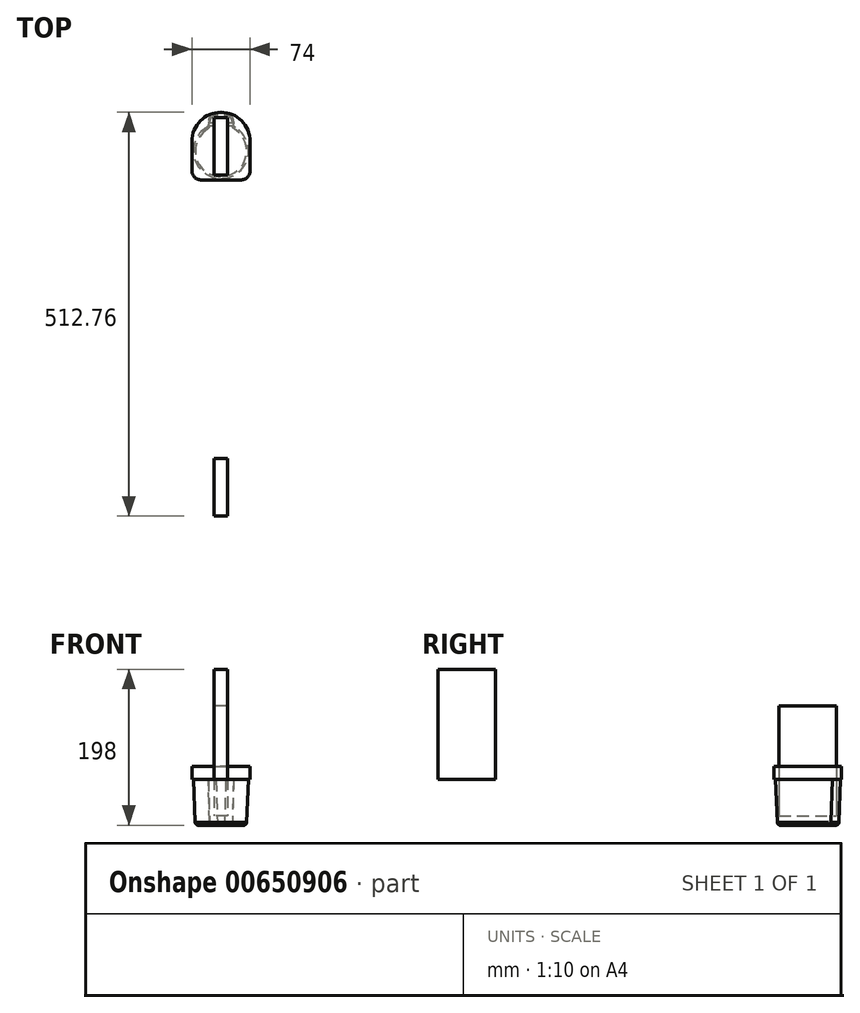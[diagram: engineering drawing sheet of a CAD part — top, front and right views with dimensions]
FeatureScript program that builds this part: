
annotation { "Feature Type Name" : "Feature", "Feature Type Description" : "" }
export const myFeature = defineFeature(function(context is Context, id is Id, definition is map)
    precondition{}
    {
        {
            var Q0;
            Q0=qCreatedBy(makeId("Top.planeOp"),FACE);
            var sketch = newSketch(context, id + "F0", { "sketchPlane" : qUnion([Q0])});
            skArc(sketch, "E0", {"start": v(37, 0) * mm, "mid": v(0, 37) * mm, "end": v(-37, 0) * mm});
            skLineSegment(sketch, "E1.top", {"start": v(-25, -49) * mm, "end": v(25, -49) * mm});
            skLineSegment(sketch, "E1.left", {"start": v(-37, 0) * mm, "end": v(-37, -37) * mm});
            skLineSegment(sketch, "E1.right", {"start": v(37, 0) * mm, "end": v(37, -37) * mm});
            skPoint(sketch, "E2.visualSharp", {"position": v(-37, -49) * mm});
            skArc(sketch, "E2.filletArc", {"start": v(-37, -37) * mm, "mid": v(-33.49, -45.49) * mm, "end": v(-25, -49) * mm});
            skPoint(sketch, "E3.visualSharp", {"position": v(37, -49) * mm});
            skArc(sketch, "E3.filletArc", {"start": v(25, -49) * mm, "mid": v(33.49, -45.49) * mm, "end": v(37, -37) * mm});
            skSolve(sketch);
        }
        {
            var Q0;
            Q0=makeQuery(id+"F0.imprint","IMPRINT",FACE,{"disambiguationData":[TD([[makeQuery(id+"F0.imprint","IMPRINT",EDGE,{"derivedFrom":sQuery(id+"F0.wireOp",EDGE,"E0")}),1.0]])]});
            extrude(context, id + "F1", {"entities" : qUnion([Q0]), "depth" : 17 * mm, "offsetDistance" : 25 * mm});
        }
        {
            var Q0;
            Q0=qCreatedBy(makeId("Top.planeOp"),FACE);
            cPlane(context, id + "F2", {"entities" : qUnion([Q0]), "cplaneType" : CPlaneType.OFFSET, "offset" : 58 * mm, "oppositeDirection" : true, "width" : 150 * mm, "height" : 150 * mm});
        }
        {
            var Q0;
            Q0=qCreatedBy(makeId("Top.planeOp"),FACE);
            var sketch = newSketch(context, id + "F3", { "sketchPlane" : qUnion([Q0])});
            skArc(sketch, "E4", {"start": v(-16, 19.13) * mm, "mid": v(0, -47) * mm, "end": v(16, 19.13) * mm});
            skLineSegment(sketch, "E5.bottom", {"start": v(6, 35.5) * mm, "end": v(-6, 35.5) * mm});
            skLineSegment(sketch, "E5.left", {"start": v(16, 25.5) * mm, "end": v(16, 19.13) * mm});
            skLineSegment(sketch, "E5.right", {"start": v(-16, 25.5) * mm, "end": v(-16, 19.13) * mm});
            skPoint(sketch, "E5.middle", {"position": v(0, 16.75) * mm});
            skPoint(sketch, "E6.visualSharp", {"position": v(-16, 35.5) * mm});
            skArc(sketch, "E6.filletArc", {"start": v(-6, 35.5) * mm, "mid": v(-13.07, 32.57) * mm, "end": v(-16, 25.5) * mm});
            skPoint(sketch, "E7.visualSharp", {"position": v(16, 35.5) * mm});
            skArc(sketch, "E7.filletArc", {"start": v(16, 25.5) * mm, "mid": v(13.07, 32.57) * mm, "end": v(6, 35.5) * mm});
            skPoint(sketch, "E5.top.end.orphan", {"position": v(-16, -2) * mm});
            skPoint(sketch, "E5.top.start.orphan", {"position": v(16, -2) * mm});
            skSolve(sketch);
        }
        {
            var Q0;
            Q0=qCreatedBy(id+"F2.planeOp",FACE);
            var sketch = newSketch(context, id + "F4", { "sketchPlane" : qUnion([Q0])});
            skArc(sketch, "E8", {"start": v(-14.5, 17.09) * mm, "mid": v(0, -44.5) * mm, "end": v(14.5, 17.09) * mm});
            skLineSegment(sketch, "E9.bottom", {"start": v(4.5, 33.5) * mm, "end": v(-4.5, 33.5) * mm});
            skLineSegment(sketch, "E9.left", {"start": v(14.5, 23.5) * mm, "end": v(14.5, 17.09) * mm});
            skLineSegment(sketch, "E9.right", {"start": v(-14.5, 23.5) * mm, "end": v(-14.5, 17.09) * mm});
            skPoint(sketch, "E9.middle", {"position": v(0, 13.85) * mm});
            skPoint(sketch, "E10.visualSharp", {"position": v(-14.5, 33.5) * mm});
            skArc(sketch, "E10.filletArc", {"start": v(-4.5, 33.5) * mm, "mid": v(-11.57, 30.57) * mm, "end": v(-14.5, 23.5) * mm});
            skPoint(sketch, "E11.visualSharp", {"position": v(14.5, 33.5) * mm});
            skArc(sketch, "E11.filletArc", {"start": v(14.5, 23.5) * mm, "mid": v(11.57, 30.57) * mm, "end": v(4.5, 33.5) * mm});
            skPoint(sketch, "E9.top.end.orphan", {"position": v(-14.5, -5.8) * mm});
            skPoint(sketch, "E12.orphan", {"position": v(14.5, -5.8) * mm});
            skSolve(sketch);
        }
        {
            var Q1;
            Q1=makeQuery(id+"F3.imprint","IMPRINT",FACE,{"disambiguationData":[TD([[makeQuery(id+"F3.imprint","IMPRINT",EDGE,{"derivedFrom":sQuery(id+"F3.wireOp",EDGE,"E4")}),1.0]])]});
            var Q2;
            Q2=makeQuery(id+"F4.imprint","IMPRINT",FACE,{"disambiguationData":[TD([[makeQuery(id+"F4.imprint","IMPRINT",EDGE,{"derivedFrom":sQuery(id+"F4.wireOp",EDGE,"E8")}),1.0]])]});
            loft(context, id + "F5", {"operationType" : NewBodyOperationType.ADD, "sheetProfilesArray" : [{ "sheetProfileEntities" : qUnion([Q1]) }, { "sheetProfileEntities" : qUnion([Q2]) }]});
        }
        {
            var Q0;
            Q0=makeQuery(id+"F5.opLoft","SWEPT_EDGE",EDGE,{"disambiguationData":[OSD([sQuery(id+"F3.wireOp",EDGE,"E4"),sQuery(id+"F3.wireOp",EDGE,"E5.right"),sQuery(id+"F4.wireOp",EDGE,"E8"),sQuery(id+"F4.wireOp",EDGE,"E9.right")])]});
            var Q1;
            Q1=makeQuery(id+"F5.opLoft","SWEPT_EDGE",EDGE,{"disambiguationData":[OSD([sQuery(id+"F3.wireOp",EDGE,"E4"),sQuery(id+"F3.wireOp",EDGE,"E5.left"),sQuery(id+"F4.wireOp",EDGE,"E8"),sQuery(id+"F4.wireOp",EDGE,"E9.left")])]});
            fillet(context, id + "F6", {"entities" : qUnion([Q0, Q1]), "radius" : 5 * mm, "tangentPropagation" : true, "allowEdgeOverflow" : false});
        }
        {
            var Q0;
            Q0=makeQuery(id+"F5.opLoft","MID_CAP_EDGE",EDGE,{"disambiguationData":[OSD([sQuery(id+"F4.wireOp",EDGE,"E8"),sQuery(id+"F4.wireOp",EDGE,"E9.left"),sQuery(id+"F4.wireOp",EDGE,"E9.right")])],"capPos":1.0});
            fillet(context, id + "F7", {"entities" : qUnion([Q0]), "radius" : 4 * mm, "tangentPropagation" : true, "allowEdgeOverflow" : false});
        }
        {
            var Q0;
            Q0=qCreatedBy(makeId("Top.planeOp"),FACE);
            var sketch = newSketch(context, id + "F8", { "sketchPlane" : qUnion([Q0])});
            skLineSegment(sketch, "E13.bottom", {"start": v(8.5, -475.76) * mm, "end": v(-8.5, -475.76) * mm});
            skLineSegment(sketch, "E13.top", {"start": v(8.5, -402.76) * mm, "end": v(-8.5, -402.76) * mm});
            skLineSegment(sketch, "E13.left", {"start": v(8.5, -475.76) * mm, "end": v(8.5, -402.76) * mm});
            skLineSegment(sketch, "E13.right", {"start": v(-8.5, -475.76) * mm, "end": v(-8.5, -402.76) * mm});
            skPoint(sketch, "E13.middle", {"position": v(0, -439.26) * mm});
            skSolve(sketch);
        }
        {
            var Q0;
            Q0=makeQuery(id+"F8.imprint","IMPRINT",FACE,{"disambiguationData":[TD([[makeQuery(id+"F8.imprint","IMPRINT",EDGE,{"derivedFrom":sQuery(id+"F8.wireOp",EDGE,"E13.bottom")}),-1.0]])]});
            extrude(context, id + "F9", {"entities" : qUnion([Q0]), "depth" : 140 * mm, "offsetDistance" : 25 * mm});
        }
        {
            var Q0;
            Q0=makeQuery(id+"F9.opExtrude","SWEPT_BODY",BODY,{"disambiguationData":[OSD([sQuery(id+"F8.wireOp",EDGE,"E13.bottom"),sQuery(id+"F8.wireOp",EDGE,"E13.top"),sQuery(id+"F8.wireOp",EDGE,"E13.left"),sQuery(id+"F8.wireOp",EDGE,"E13.right")])]});
            transform(context, id + "F10", {"entities" : qUnion([Q0]), "transformType" : TransformType.TRANSLATION_3D, "dx" : 0 * mm, "dy" : 433.3 * mm, "dz" : -46.2 * mm, "makeCopy" : true});
        }
    });
